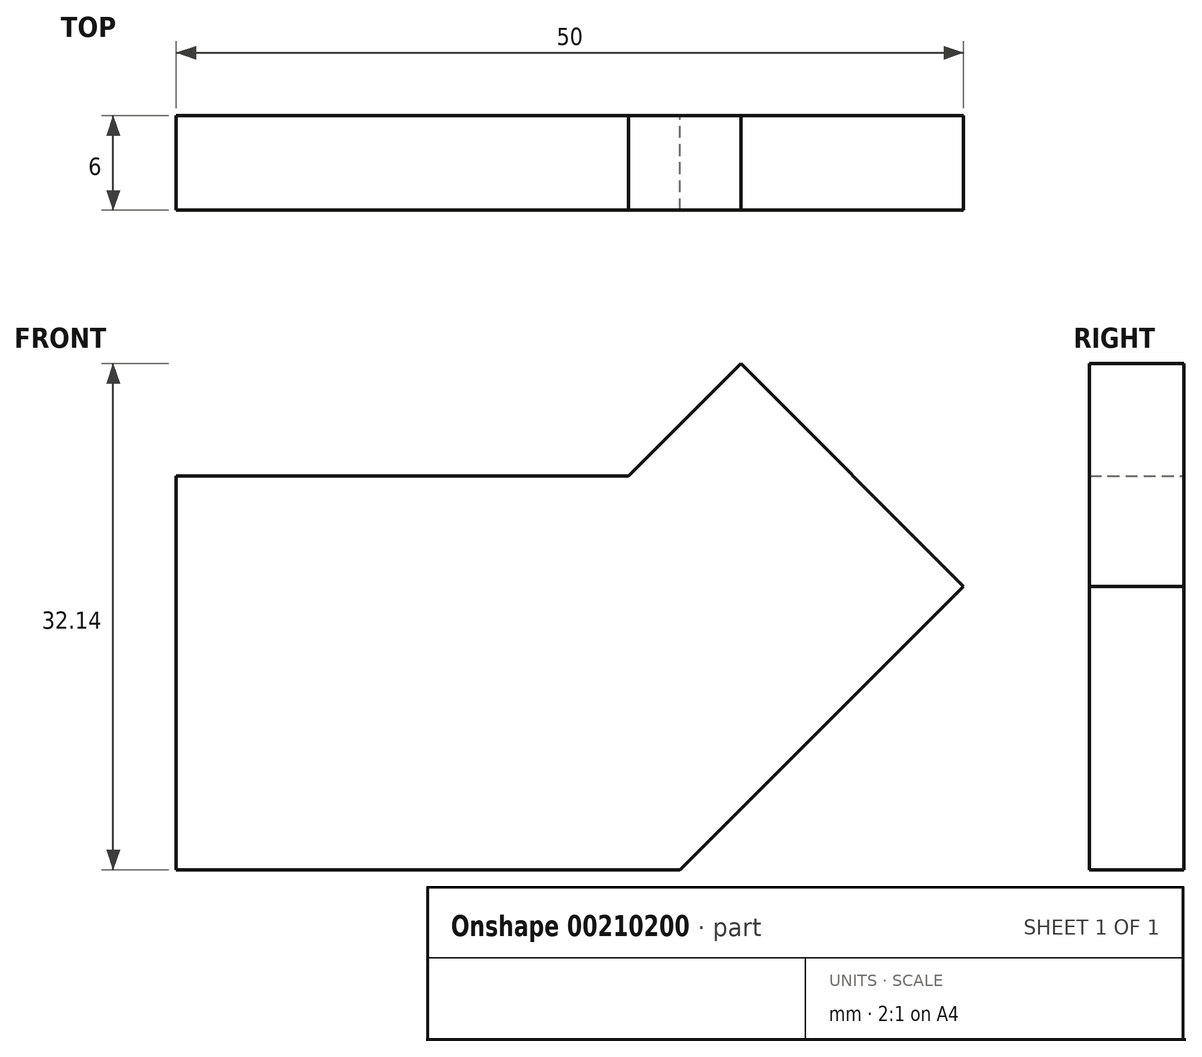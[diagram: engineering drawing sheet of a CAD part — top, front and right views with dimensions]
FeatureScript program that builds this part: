
annotation { "Feature Type Name" : "Feature", "Feature Type Description" : "" }
export const myFeature = defineFeature(function(context is Context, id is Id, definition is map)
    precondition{}
    {
        {
            var Q0;
            Q0=qCreatedBy(makeId("Front.planeOp"),FACE);
            var sketch = newSketch(context, id + "F0", { "sketchPlane" : qUnion([Q0])});
            skLineSegment(sketch, "E0", {"start": v(0, 0) * mm, "end": v(32, 0) * mm});
            skLineSegment(sketch, "E1", {"start": v(32, 0) * mm, "end": v(50, 18) * mm});
            skLineSegment(sketch, "E2", {"start": v(50, 18) * mm, "end": v(35.86, 32.14) * mm});
            skLineSegment(sketch, "E3", {"start": v(35.86, 32.14) * mm, "end": v(28.72, 25) * mm});
            skLineSegment(sketch, "E4", {"start": v(28.72, 25) * mm, "end": v(0, 25) * mm});
            skLineSegment(sketch, "E5", {"start": v(0, 25) * mm, "end": v(0, 0) * mm});
            skSolve(sketch);
        }
        {
            var Q0;
            Q0 = qSketchRegion(id + "F0", true);
            extrude(context, id + "F1", {"entities" : qUnion([Q0]), "depth" : 6 * mm});
        }
    });
